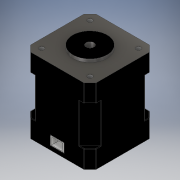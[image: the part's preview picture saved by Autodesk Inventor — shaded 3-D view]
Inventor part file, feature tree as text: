
AUTODESK INVENTOR PART (.ipt)
format: ipt  version: 2018 (Build 220112000, 112)  size: 330,240 bytes
history: native  units: in
note: dims shown in document units (in); Inventor stores cm internally (conversion verified against a paired STEP export)
features: extrude x9, sketch x9, thread x4, plane x1, fillet x1, projected_geometry x1
ambient origin geometry x8: Origin, YZ Plane, XZ Plane, XY Plane, X Axis, Y Axis, Z Axis, Center Point
bodies: Solid1 (feature_tree)
feature tree (25):
  extrude  "Extrusion1"  Depth=1.6535in
  plane  "Work Plane1"
  extrude  "Extrusion2"  Depth=0.6693in
  extrude  "Extrusion3"  Depth=1.8898in
  extrude  "Extrusion4"  Depth=0.9843in TaperAngle=0.0deg
  extrude  "Extrusion5"  Depth=0.0787in TaperAngle=0.0deg
  thread  "Thread1"  [1 undecoded]
  thread  "Thread2"  [1 undecoded]
  thread  "Thread3"  [1 undecoded]
  thread  "Thread4"  [1 undecoded]
  extrude  "Extrusion6"  Depth=0.1772in TaperAngle=0.0deg
  extrude  "Extrusion7"  Depth=0.3937in TaperAngle=0.0deg
  fillet  "Fillet1"  Radius=0.3937in
  extrude  "Extrusion8"  Depth=0.3937in TaperAngle=0.0deg
  extrude  "Extrusion9"  Depth=0.2362in
  sketch  "Sketch1"  dims[d0=1.6535in d1=1.6535in]
  sketch  "Sketch2"  dims[d2=0.6693in d3=0.6693in]
  projected_geometry  "Projected Loop1"
  sketch  "Sketch3"  dims[d4=1.8898in d5=0.0in d6=0.5512in]
  sketch  "Sketch4"  dims[d7=0.5512in d8=0.9843in d9=0.0in]
  sketch  "Sketch5"  dims[d10=0.8661in d11=0.0787in d12=0.0in d13=0.1969in d14=2.7662in d15=0.0in d16=0.1181in d17=0.6102in]
  sketch  "Sketch6"  dims[d18=0.6102in d19=0.1772in d20=0.0in]
  sketch  "Sketch7"  dims[d21=0.3937in d22=0.0in d23=0.3937in d24=0.0in d25=0.3937in d26=0.0in]
  sketch  "Sketch8"  dims[d27=0.3937in d28=0.0in d29=0.3937in d30=0.0in]
  sketch  "Sketch9"  dims[d31=0.2362in d32=0.2362in d33=0.2362in d35=0.2362in d36=0.0787in d37=0.0in d38=0.0118in d39=0.3543in d40=0.2362in d41=0.0984in d42=0.1969in d43=0.0in d44=0.1969in d45=0.0in]
note: 4 required parameter values undecoded (feature->parameter linkage not recoverable at this tier; creation-order binding heuristic only, values carry confidence <= 0.55)
